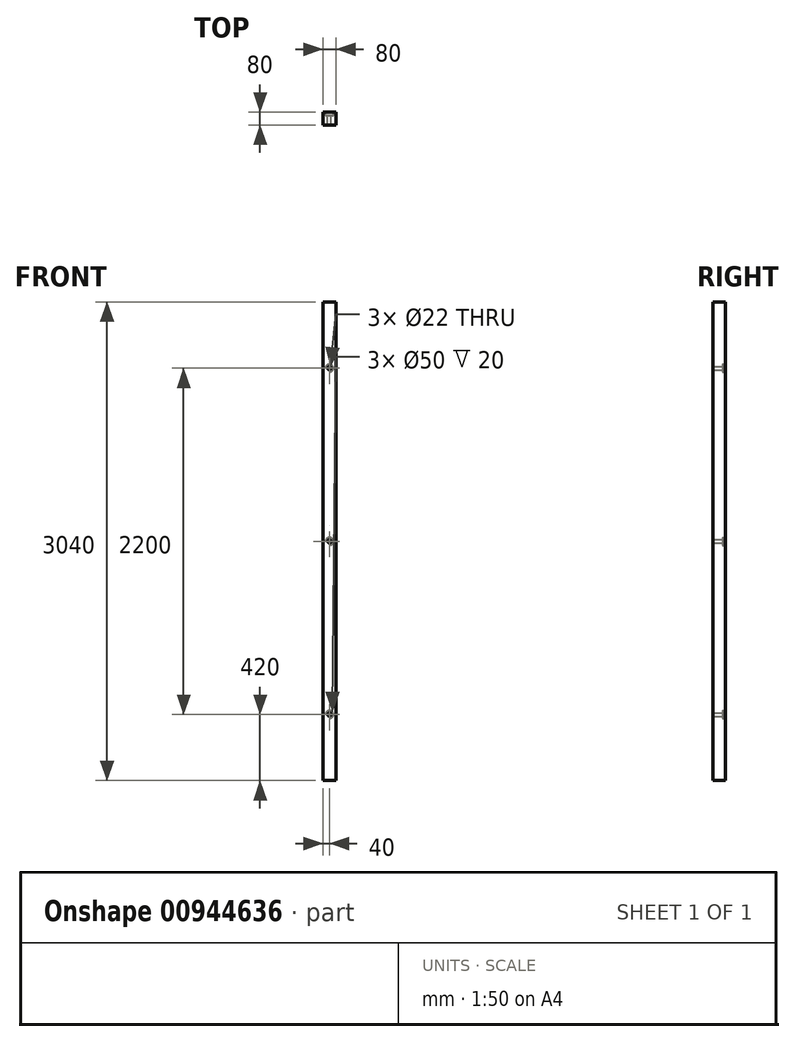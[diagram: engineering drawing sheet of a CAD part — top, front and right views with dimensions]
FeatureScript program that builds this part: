
annotation { "Feature Type Name" : "Feature", "Feature Type Description" : "" }
export const myFeature = defineFeature(function(context is Context, id is Id, definition is map)
    precondition{}
    {
        {
            var Q0;
            Q0=qCreatedBy(makeId("Top.planeOp"),FACE);
            var sketch = newSketch(context, id + "F0", { "sketchPlane" : qUnion([Q0])});
            skLineSegment(sketch, "E0.bottom", {"start": v(0, 0) * mm, "end": v(80, 0) * mm});
            skLineSegment(sketch, "E0.top", {"start": v(0, 80) * mm, "end": v(80, 80) * mm});
            skLineSegment(sketch, "E0.left", {"start": v(0, 0) * mm, "end": v(0, 80) * mm});
            skLineSegment(sketch, "E0.right", {"start": v(80, 0) * mm, "end": v(80, 80) * mm});
            skSolve(sketch);
        }
        {
            var Q0;
            Q0=makeQuery(id+"F0.imprint","IMPRINT",FACE,{"disambiguationData":[TD([[makeQuery(id+"F0.imprint","IMPRINT",EDGE,{"derivedFrom":sQuery(id+"F0.wireOp",EDGE,"E0.bottom")}),1.0]])]});
            extrude(context, id + "F1", {"entities" : qUnion([Q0]), "depth" : 3040 * mm, "offsetDistance" : 25 * mm});
        }
        {
            var Q0;
            Q0=makeQuery(id+"F1.opExtrude","SWEPT_FACE",FACE,{"disambiguationData":[OSD([sQuery(id+"F0.wireOp",EDGE,"E0.top")])]});
            var sketch = newSketch(context, id + "F2", { "sketchPlane" : qUnion([Q0])});
            skPoint(sketch, "E1", {"position": v(-40, 2620) * mm});
            skLineSegment(sketch, "E2", {"start": v(-40, 3040) * mm, "end": v(-40, 2620) * mm, "construction": true});
            skLineSegment(sketch, "E3", {"start": v(-40, 2620) * mm, "end": v(0, 2620) * mm, "construction": true});
            skLineSegment(sketch, "E4", {"start": v(0, 2620) * mm, "end": v(-40, 2620) * mm, "construction": true});
            skLineSegment(sketch, "E5", {"start": v(-40, 2620) * mm, "end": v(-80, 2620) * mm, "construction": true});
            skLineSegment(sketch, "E6", {"start": v(-80, 1520) * mm, "end": v(0, 1520) * mm, "construction": true});
            skLineSegment(sketch, "E7", {"start": v(-40, 0) * mm, "end": v(-40, 420) * mm, "construction": true});
            skLineSegment(sketch, "E8", {"start": v(-40, 420) * mm, "end": v(-80, 420) * mm, "construction": true});
            skLineSegment(sketch, "E9", {"start": v(-40, 420) * mm, "end": v(0, 420) * mm, "construction": true});
            skPoint(sketch, "E10", {"position": v(-40, 1520) * mm});
            skSolve(sketch);
        }
        {
            var Q0;
            Q0=sQuery(id+"F2.wireOp",VERTEX,"E1");
            var Q1;
            Q1=sQuery(id+"F2.wireOp",VERTEX,"E7.end");
            var Q2;
            Q2=sQuery(id+"F2.wireOp",VERTEX,"E10");
            var Q3;
            Q3=makeQuery(id+"F1.opExtrude","SWEPT_BODY",BODY,{"disambiguationData":[OSD([sQuery(id+"F0.wireOp",EDGE,"E0.bottom"),sQuery(id+"F0.wireOp",EDGE,"E0.top"),sQuery(id+"F0.wireOp",EDGE,"E0.left"),sQuery(id+"F0.wireOp",EDGE,"E0.right")])]});
            hole(context, id + "F3", {"style" : HoleStyle.C_BORE, "endStyle" : HoleEndStyle.BLIND, "holeDiameter" : 22 * mm, "cBoreDiameter" : 50 * mm, "cBoreDepth" : 20 * mm, "majorDiameter" : 20 * mm, "holeDepth" : 100 * mm, "isTappedThrough" : true, "tappedDepth" : 92.5 * mm, "tapClearance" : 3, "locations" : qUnion([Q0, Q1, Q2]), "scope" : qUnion([Q3])});
        }
    });
